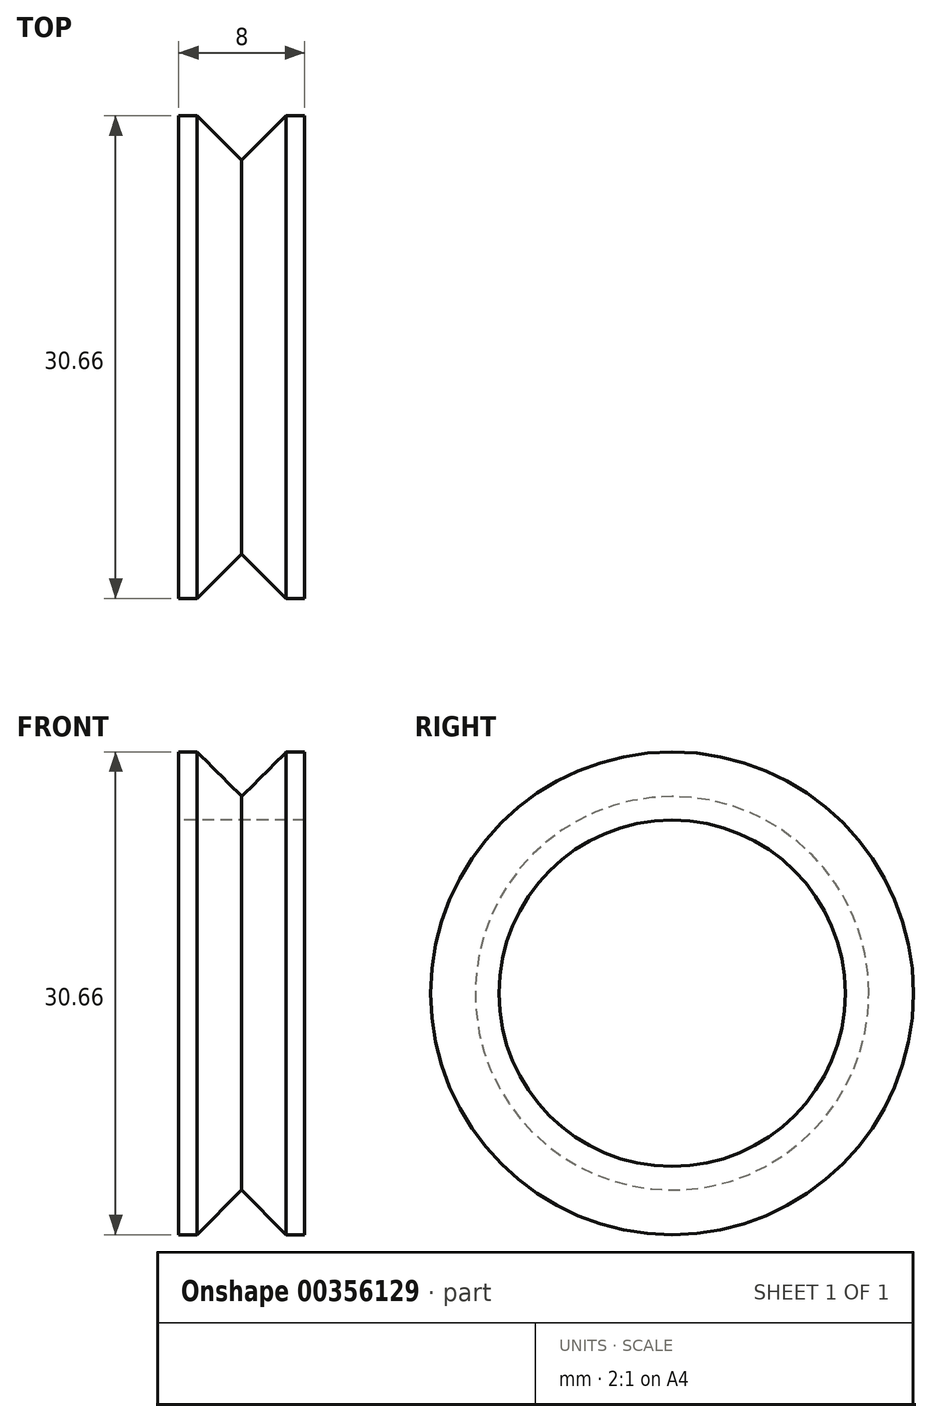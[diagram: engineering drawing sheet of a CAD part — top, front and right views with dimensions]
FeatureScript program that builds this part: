
annotation { "Feature Type Name" : "Feature", "Feature Type Description" : "" }
export const myFeature = defineFeature(function(context is Context, id is Id, definition is map)
    precondition{}
    {
        {
            var Q0;
            Q0=qCreatedBy(makeId("Front.planeOp"),FACE);
            var sketch = newSketch(context, id + "F0", { "sketchPlane" : qUnion([Q0])});
            skLineSegment(sketch, "E0", {"start": v(0, 0) * mm, "end": v(0, 6.36) * mm, "construction": true});
            skLineSegment(sketch, "E1", {"start": v(0, 1.5) * mm, "end": v(2.83, 4.33) * mm});
            skLineSegment(sketch, "E2.MirrorCS", {"start": v(0, 1.5) * mm, "end": v(-2.83, 4.33) * mm});
            skLineSegment(sketch, "E3", {"start": v(4, 0) * mm, "end": v(4, 4.33) * mm});
            skLineSegment(sketch, "E4", {"start": v(0, -11) * mm, "end": v(4, -11) * mm, "construction": true});
            skLineSegment(sketch, "E5", {"start": v(-4, 0) * mm, "end": v(4, 0) * mm});
            skLineSegment(sketch, "E6", {"start": v(2.83, 4.33) * mm, "end": v(4, 4.33) * mm});
            skLineSegment(sketch, "E7.MirrorCS", {"start": v(-4, 0) * mm, "end": v(-4, 4.33) * mm});
            skLineSegment(sketch, "E8.MirrorCS", {"start": v(-2.83, 4.33) * mm, "end": v(-4, 4.33) * mm});
            skSolve(sketch);
        }
        {
            var Q0;
            Q0=makeQuery(id+"F0.imprint","IMPRINT",FACE,{"disambiguationData":[TD([[makeQuery(id+"F0.imprint","IMPRINT",EDGE,{"derivedFrom":sQuery(id+"F0.wireOp",EDGE,"E1")}),-1.0]])]});
            var Q1;
            Q1=sQuery(id+"F0.wireOp",EDGE,"E4");
            revolve(context, id + "F1", {"entities" : qUnion([Q0]), "axis" : qUnion([Q1]), "revolveType" : RevolveType.FULL});
        }
    });
